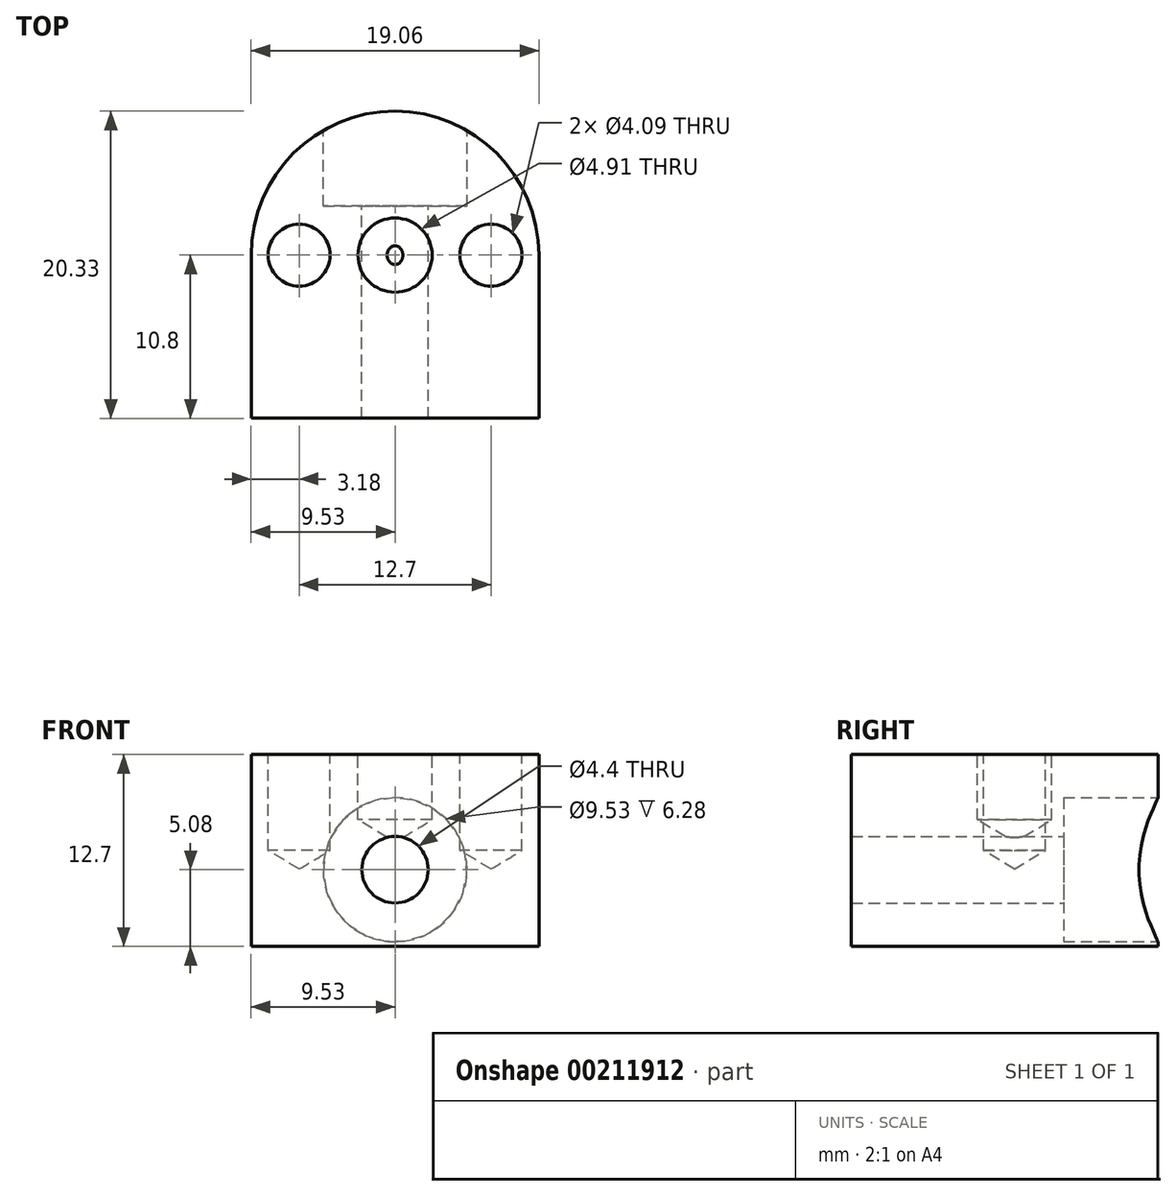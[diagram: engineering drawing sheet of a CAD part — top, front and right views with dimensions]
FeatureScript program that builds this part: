
annotation { "Feature Type Name" : "Feature", "Feature Type Description" : "" }
export const myFeature = defineFeature(function(context is Context, id is Id, definition is map)
    precondition{}
    {
        {
            var Q0;
            Q0=qCreatedBy(makeId("Top.planeOp"),FACE);
            var sketch = newSketch(context, id + "F0", { "sketchPlane" : qUnion([Q0])});
            skArc(sketch, "E0", {"start": v(9.53, 0) * mm, "mid": v(0, 9.53) * mm, "end": v(-9.53, 0) * mm});
            skLineSegment(sketch, "E1.top", {"start": v(-9.52, -10.8) * mm, "end": v(9.52, -10.8) * mm});
            skLineSegment(sketch, "E1.left", {"start": v(-9.53, 0) * mm, "end": v(-9.53, -10.8) * mm});
            skLineSegment(sketch, "E1.right", {"start": v(9.53, 0) * mm, "end": v(9.53, -10.8) * mm});
            skSolve(sketch);
        }
        {
            var Q0;
            Q0=makeQuery(id+"F0.imprint","IMPRINT",FACE,{"disambiguationData":[TD([[makeQuery(id+"F0.imprint","IMPRINT",EDGE,{"derivedFrom":sQuery(id+"F0.wireOp",EDGE,"E0")}),1.0]])]});
            extrude(context, id + "F1", {"entities" : qUnion([Q0]), "oppositeDirection" : true, "depth" : 12.7 * mm});
        }
        {
            var Q0;
            Q0=makeQuery(id+"F1.opExtrude","CAP_FACE",FACE,{"disambiguationData":[OSD([sQuery(id+"F0.wireOp",EDGE,"E0"),sQuery(id+"F0.wireOp",EDGE,"E1.top"),sQuery(id+"F0.wireOp",EDGE,"E1.left"),sQuery(id+"F0.wireOp",EDGE,"E1.right")])],"isStart":true});
            var sketch = newSketch(context, id + "F2", { "sketchPlane" : qUnion([Q0])});
            skPoint(sketch, "E2", {"position": v(-6.35, 0) * mm});
            skPoint(sketch, "E3", {"position": v(0, 0) * mm});
            skPoint(sketch, "E4", {"position": v(6.35, 0) * mm});
            skLineSegment(sketch, "E5", {"start": v(-6.35, 0) * mm, "end": v(6.35, 0) * mm});
            skSolve(sketch);
        }
        {
            var Q0;
            Q0=sQuery(id+"F2.wireOp",VERTEX,"E3");
            var Q1;
            Q1=makeQuery(id+"F1.opExtrude","SWEPT_BODY",BODY,{"disambiguationData":[OSD([sQuery(id+"F0.wireOp",EDGE,"E0"),sQuery(id+"F0.wireOp",EDGE,"E1.top"),sQuery(id+"F0.wireOp",EDGE,"E1.left"),sQuery(id+"F0.wireOp",EDGE,"E1.right")])]});
            hole(context, id + "F3", {"style" : HoleStyle.SIMPLE, "endStyle" : HoleEndStyle.BLIND, "standardTappedOrClearance" : lookupTablePath({ "standard" : "ANSI", "size" : "#10 (0.2)", "type" : "Drilled" }), "standardBlindInLast" : lookupTablePath({ "standard" : "ANSI", "size" : "#10", "type" : "Drilled" }), "holeDiameter" : 4.9 * mm, "holeDepth" : 4.32 * mm, "locations" : qUnion([Q0]), "scope" : qUnion([Q1])});
        }
        {
            var Q0;
            Q0=sQuery(id+"F2.wireOp",VERTEX,"E4");
            var Q1;
            Q1=sQuery(id+"F2.wireOp",VERTEX,"E2");
            var Q2;
            Q2=makeQuery(id+"F1.opExtrude","SWEPT_BODY",BODY,{"disambiguationData":[OSD([sQuery(id+"F0.wireOp",EDGE,"E0"),sQuery(id+"F0.wireOp",EDGE,"E1.top"),sQuery(id+"F0.wireOp",EDGE,"E1.left"),sQuery(id+"F0.wireOp",EDGE,"E1.right")])]});
            hole(context, id + "F4", {"style" : HoleStyle.SIMPLE, "endStyle" : HoleEndStyle.BLIND, "standardTappedOrClearance" : lookupTablePath({ "standard" : "ANSI", "size" : "#20 (0.16)", "type" : "Drilled" }), "standardBlindInLast" : lookupTablePath({ "standard" : "ANSI", "size" : "#20", "type" : "Drilled" }), "holeDiameter" : 4.1 * mm, "holeDepth" : 6.35 * mm, "locations" : qUnion([Q0, Q1]), "scope" : qUnion([Q2])});
        }
        {
            var Q0;
            Q0=qCreatedBy(makeId("Front.planeOp"),FACE);
            cPlane(context, id + "F5", {"entities" : qUnion([Q0]), "cplaneType" : CPlaneType.OFFSET, "offset" : 9.52 * mm, "oppositeDirection" : true, "width" : 152.4 * mm, "height" : 152.4 * mm});
        }
        {
            var Q0;
            Q0=qCreatedBy(id+"F5.planeOp",FACE);
            var sketch = newSketch(context, id + "F6", { "sketchPlane" : qUnion([Q0])});
            skLineSegment(sketch, "E6", {"start": v(-5, -7.62) * mm, "end": v(5, -7.62) * mm});
            skPoint(sketch, "E7", {"position": v(0, -7.62) * mm});
            skSolve(sketch);
        }
        {
            var Q0;
            Q0=sQuery(id+"F6.wireOp",VERTEX,"E7");
            var Q1;
            Q1=makeQuery(id+"F1.opExtrude","SWEPT_BODY",BODY,{"disambiguationData":[OSD([sQuery(id+"F0.wireOp",EDGE,"E0"),sQuery(id+"F0.wireOp",EDGE,"E1.top"),sQuery(id+"F0.wireOp",EDGE,"E1.left"),sQuery(id+"F0.wireOp",EDGE,"E1.right")])]});
            hole(context, id + "F7", {"style" : HoleStyle.C_BORE, "endStyle" : HoleEndStyle.THROUGH, "oppositeDirection" : true, "holeDiameter" : 4.4 * mm, "cBoreDiameter" : 9.52 * mm, "cBoreDepth" : 5 * mm, "locations" : qUnion([Q0]), "scope" : qUnion([Q1]), "isTappedThrough" : true});
        }
    });
